# Revit family: 500_Slenderline_Sliding_Window_XOX_Standard
name_source: partatom
category: Windows
revit_build: Autodesk Revit 2014 (Build: 20130308_1515(x64)
units: mm (PartAtom-declared; Revit-internal decimal feet)

## types (56) — shared parameters
Centered In Wall = Yes
Custom Sash Width Middle = 500 mm  [stored 1.64042 ft]
Default Sill Height = 800 mm  [stored 2.62467 ft]
Description = Slenderline Sliding Window
Equal Sash Width = Yes
Frame Thickness = 54 mm
Heavy Duty Interlocker = No
Limit Sash Height Max = 1500 mm  [stored 4.92126 ft]
Limit Sash Height Min = 300 mm  [stored 0.984252 ft]
Limit Sash Width Max = 750 mm  [stored 2.46063 ft]
Limit Sash Width Min = 300 mm  [stored 0.984252 ft]
Limit Window Height Max = 1575 mm
Limit Window Height Min = 375 mm
Limit Window Width Max = 2270 mm  [stored 7.44751 ft]
Limit Window Width Min = 920 mm  [stored 3.01837 ft]
Manufacturer = Crealco
Model = 500
Sash Frame Seal = 1 mm  [stored 0.00328084 ft]
Sash Rail Fore Aft Spacing = 2 mm  [stored 0.00656168 ft]
Standard Interlocker = Yes
URL = www.crealco.co.za
Wall Closure = By host
zero-valued in all types: Custom Frame Offset From Exterior, Is Heavy Duty Mullion

## per-type parameters (varying)
| type | Area Middle Sash Glazing | Area Side Sash Glazing | Clearvue SHGC Value | Clearvue U Value | Custom Windload | Custom Window Height | Custom Window Width | Energy Advantage SHGC Value | Energy Advantage U Value | Height | Intruderprufe LowE SHGC Value | Intruderprufe LowE U Value | Intruderprufe SHGC Value | Intruderprufe U Value | Limit Sash Width Middle Max | Limit Sash Width Middle Min | Max Pane Area | Sash Height | Sash Width Middle | Sash Width Sides | Width | Windload Design |
| 500SW-0906XOX-1000Pa | 0.12 m² | 0.12 m² | 0.563 | 6.18 | 1000 mm  [stored 3.28084 ft] | 590 mm  [stored 1.9357 ft] | 890 mm  [stored 2.91995 ft] | 0.505 | 5.1 | 590 mm  [stored 1.9357 ft] | 0.427 | 4.69 | 0.534 | 6.05 | 300 mm  [stored 0.984252 ft] | 300 mm  [stored 0.984252 ft] | 0.12 m² | 515 mm | 300 mm  [stored 0.984252 ft] | 300 mm  [stored 0.984252 ft] | 920 mm  [stored 3.01837 ft] | 1000 mm  [stored 3.28084 ft] |
| 500SW-1206XOX-1000Pa | 0.16 m² | 0.16 m² | 0.578 | 6.19 | 1000 mm  [stored 3.28084 ft] | 590 mm  [stored 1.9357 ft] | 1190 mm  [stored 3.9042 ft] | 0.519 | 5 | 590 mm  [stored 1.9357 ft] | 0.439 | 4.7 | 0.549 | 6.06 | 570 mm  [stored 1.87008 ft] | 300 mm  [stored 0.984252 ft] | 0.16 m² | 515 mm | 390 mm | 390 mm | 1190 mm  [stored 3.9042 ft] | 1000 mm  [stored 3.28084 ft] |
| 500SW-1506XOX-1000Pa | 0.2 m² | 0.2 m² | 0.588 | 6.2 | 1000 mm  [stored 3.28084 ft] | 590 mm  [stored 1.9357 ft] | 1490 mm  [stored 4.88845 ft] | 0.527 | 4.93 | 590 mm  [stored 1.9357 ft] | 0.446 | 4.71 | 0.558 | 6.07 | 750 mm  [stored 2.46063 ft] | 300 mm  [stored 0.984252 ft] | 0.2 m² | 515 mm | 490 mm | 490 mm | 1490 mm  [stored 4.88845 ft] | 1000 mm  [stored 3.28084 ft] |
| 500SW-1806XOX-1000Pa | 0.25 m² | 0.25 m² | 0.594 | 6.2 | 1000 mm  [stored 3.28084 ft] | 590 mm  [stored 1.9357 ft] | 1790 mm  [stored 5.8727 ft] | 0.532 | 4.89 | 590 mm  [stored 1.9357 ft] | 0.451 | 4.71 | 0.564 | 6.07 | 750 mm  [stored 2.46063 ft] | 300 mm  [stored 0.984252 ft] | 0.25 m² | 515 mm | 590 mm  [stored 1.9357 ft] | 590 mm  [stored 1.9357 ft] | 1790 mm  [stored 5.8727 ft] | 1000 mm  [stored 3.28084 ft] |
| 500SW-2106XOX-1000Pa | 0.29 m² | 0.29 m² | 0.598 | 6.21 | 1000 mm  [stored 3.28084 ft] | 590 mm  [stored 1.9357 ft] | 2090 mm  [stored 6.85696 ft] | 0.536 | 4.86 | 590 mm  [stored 1.9357 ft] | 0.455 | 4.71 | 0.569 | 6.08 | 750 mm  [stored 2.46063 ft] | 570 mm  [stored 1.87008 ft] | 0.29 m² | 515 mm | 690 mm | 690 mm | 2090 mm  [stored 6.85696 ft] | 1000 mm  [stored 3.28084 ft] |
| 500SW-0909XOX-1000Pa | 0.2 m² | 0.2 m² | 0.631 | 6.09 | 1000 mm  [stored 3.28084 ft] | 890 mm  [stored 2.91995 ft] | 890 mm  [stored 2.91995 ft] | 0.566 | 4.88 | 890 mm  [stored 2.91995 ft] | 0.476 | 4.61 | 0.599 | 5.95 | 300 mm  [stored 0.984252 ft] | 300 mm  [stored 0.984252 ft] | 0.2 m² | 815 mm | 300 mm  [stored 0.984252 ft] | 300 mm  [stored 0.984252 ft] | 920 mm  [stored 3.01837 ft] | 1000 mm  [stored 3.28084 ft] |
| 500SW-1209XOX-1000Pa | 0.27 m² | 0.27 m² | 0.649 | 6.1 | 1000 mm  [stored 3.28084 ft] | 890 mm  [stored 2.91995 ft] | 1190 mm  [stored 3.9042 ft] | 0.581 | 4.75 | 890 mm  [stored 2.91995 ft] | 0.493 | 4.63 | 0.616 | 5.97 | 570 mm  [stored 1.87008 ft] | 300 mm  [stored 0.984252 ft] | 0.27 m² | 815 mm | 390 mm | 390 mm | 1190 mm  [stored 3.9042 ft] | 1000 mm  [stored 3.28084 ft] |
| 500SW-1509XOX-1000Pa | 0.34 m² | 0.34 m² | 0.659 | 6.1 | 1000 mm  [stored 3.28084 ft] | 890 mm  [stored 2.91995 ft] | 1490 mm  [stored 4.88845 ft] | 0.59 | 4.67 | 890 mm  [stored 2.91995 ft] | 0.501 | 4.63 | 0.626 | 5.97 | 750 mm  [stored 2.46063 ft] | 300 mm  [stored 0.984252 ft] | 0.34 m² | 815 mm | 490 mm | 490 mm | 1490 mm  [stored 4.88845 ft] | 1000 mm  [stored 3.28084 ft] |
| 500SW-1809XOX-1000Pa | 0.41 m² | 0.41 m² | 0.666 | 6.1 | 1000 mm  [stored 3.28084 ft] | 890 mm  [stored 2.91995 ft] | 1790 mm  [stored 5.8727 ft] | 0.596 | 4.62 | 890 mm  [stored 2.91995 ft] | 0.506 | 4.63 | 0.632 | 5.97 | 750 mm  [stored 2.46063 ft] | 300 mm  [stored 0.984252 ft] | 0.41 m² | 815 mm | 590 mm  [stored 1.9357 ft] | 590 mm  [stored 1.9357 ft] | 1790 mm  [stored 5.8727 ft] | 1000 mm  [stored 3.28084 ft] |
| 500SW-2109XOX-1000Pa | 0.49 m² | 0.49 m² | 0.671 | 6.1 | 1000 mm  [stored 3.28084 ft] | 890 mm  [stored 2.91995 ft] | 2090 mm  [stored 6.85696 ft] | 0.601 | 4.58 | 890 mm  [stored 2.91995 ft] | 0.51 | 4.63 | 0.637 | 5.97 | 750 mm  [stored 2.46063 ft] | 570 mm  [stored 1.87008 ft] | 0.49 m² | 815 mm | 690 mm | 690 mm | 2090 mm  [stored 6.85696 ft] | 1000 mm  [stored 3.28084 ft] |
| 500SW-0912XOX-1000Pa | 0.28 m² | 0.28 m² | 0.665 | 6.05 | 1000 mm  [stored 3.28084 ft] | 1190 mm  [stored 3.9042 ft] | 890 mm  [stored 2.91995 ft] | 0.596 | 4.77 | 1190 mm  [stored 3.9042 ft] | 0.505 | 4.59 | 0.631 | 5.92 | 300 mm  [stored 0.984252 ft] | 300 mm  [stored 0.984252 ft] | 0.28 m² | 1115 mm | 300 mm  [stored 0.984252 ft] | 300 mm  [stored 0.984252 ft] | 920 mm  [stored 3.01837 ft] | 1000 mm  [stored 3.28084 ft] |
| 500SW-1212XOX-1000Pa | 0.37 m² | 0.37 m² | 0.683 | 6.05 | 1000 mm  [stored 3.28084 ft] | 1190 mm  [stored 3.9042 ft] | 1190 mm  [stored 3.9042 ft] | 0.612 | 4.62 | 1190 mm  [stored 3.9042 ft] | 0.519 | 4.59 | 0.649 | 5.92 | 570 mm  [stored 1.87008 ft] | 300 mm  [stored 0.984252 ft] | 0.37 m² | 1115 mm | 390 mm | 390 mm | 1190 mm  [stored 3.9042 ft] | 1000 mm  [stored 3.28084 ft] |
| 500SW-1512XOX-1000Pa | 0.48 m² | 0.48 m² | 0.695 | 6.05 | 1000 mm  [stored 3.28084 ft] | 1190 mm  [stored 3.9042 ft] | 1490 mm  [stored 4.88845 ft] | 0.622 | 4.54 | 1190 mm  [stored 3.9042 ft] | 0.527 | 4.59 | 0.659 | 5.92 | 750 mm  [stored 2.46063 ft] | 300 mm  [stored 0.984252 ft] | 0.48 m² | 1115 mm | 490 mm | 490 mm | 1490 mm  [stored 4.88845 ft] | 1000 mm  [stored 3.28084 ft] |
| 500SW-1812XOX-1000Pa | 0.58 m² | 0.58 m² | 0.702 | 6.05 | 1000 mm  [stored 3.28084 ft] | 1190 mm  [stored 3.9042 ft] | 1790 mm  [stored 5.8727 ft] | 0.628 | 4.48 | 1190 mm  [stored 3.9042 ft] | 0.5333 | 4.59 | 0.666 | 5.92 | 750 mm  [stored 2.46063 ft] | 300 mm  [stored 0.984252 ft] | 0.58 m² | 1115 mm | 590 mm  [stored 1.9357 ft] | 590 mm  [stored 1.9357 ft] | 1790 mm  [stored 5.8727 ft] | 1000 mm  [stored 3.28084 ft] |
| 500SW-2112XOX-1000Pa | 0.69 m² | 0.69 m² | 0.707 | 6.05 | 1000 mm  [stored 3.28084 ft] | 1190 mm  [stored 3.9042 ft] | 2090 mm  [stored 6.85696 ft] | 0.633 | 4.44 | 1190 mm  [stored 3.9042 ft] | 0.537 | 4.59 | 0.671 | 5.92 | 750 mm  [stored 2.46063 ft] | 570 mm  [stored 1.87008 ft] | 0.69 m² | 1115 mm | 690 mm | 690 mm | 2090 mm  [stored 6.85696 ft] | 1000 mm  [stored 3.28084 ft] |
| 500SW-0915XOX-1000Pa | 0.36 m² | 0.36 m² | 0.685 | 6.02 | 1000 mm  [stored 3.28084 ft] | 1490 mm  [stored 4.88845 ft] | 890 mm  [stored 2.91995 ft] | 0.614 | 4.7 | 1490 mm  [stored 4.88845 ft] | 0.521 | 4.57 | 0.657 | 5.89 | 300 mm  [stored 0.984252 ft] | 300 mm  [stored 0.984252 ft] | 0.36 m² | 1415 mm  [stored 4.64239 ft] | 300 mm  [stored 0.984252 ft] | 300 mm  [stored 0.984252 ft] | 920 mm  [stored 3.01837 ft] | 1000 mm  [stored 3.28084 ft] |
| 500SW-1215XOX-1000Pa | 0.48 m² | 0.48 m² | 0.704 | 6.02 | 1000 mm  [stored 3.28084 ft] | 1490 mm  [stored 4.88845 ft] | 1190 mm  [stored 3.9042 ft] | 0.631 | 4.55 | 1490 mm  [stored 4.88845 ft] | 0.534 | 4.57 | 0.668 | 5.89 | 570 mm  [stored 1.87008 ft] | 300 mm  [stored 0.984252 ft] | 0.48 m² | 1415 mm  [stored 4.64239 ft] | 390 mm | 390 mm | 1190 mm  [stored 3.9042 ft] | 1000 mm  [stored 3.28084 ft] |
| 500SW-1515XOX-1000Pa | 0.61 m² | 0.61 m² | 0.716 | 6.02 | 1000 mm  [stored 3.28084 ft] | 1490 mm  [stored 4.88845 ft] | 1490 mm  [stored 4.88845 ft] | 0.64 | 4.46 | 1490 mm  [stored 4.88845 ft] | 0.543 | 4.57 | 0.679 | 5.89 | 750 mm  [stored 2.46063 ft] | 300 mm  [stored 0.984252 ft] | 0.61 m² | 1415 mm  [stored 4.64239 ft] | 490 mm | 490 mm | 1490 mm  [stored 4.88845 ft] | 1000 mm  [stored 3.28084 ft] |
| 500SW-1815XOX-1000Pa | 0.75 m² | 0.75 m² | 0.723 | 6.02 | 1000 mm  [stored 3.28084 ft] | 1490 mm  [stored 4.88845 ft] | 1790 mm  [stored 5.8727 ft] | 0.647 | 4.4 | 1490 mm  [stored 4.88845 ft] | 0.549 | 4.57 | 0.686 | 5.89 | 750 mm  [stored 2.46063 ft] | 300 mm  [stored 0.984252 ft] | 0.75 m² | 1415 mm  [stored 4.64239 ft] | 590 mm  [stored 1.9357 ft] | 590 mm  [stored 1.9357 ft] | 1790 mm  [stored 5.8727 ft] | 1000 mm  [stored 3.28084 ft] |
| 500SW-2115XOX-1000Pa | 0.88 m² | 0.88 m² | 0.729 | 6.02 | 1000 mm  [stored 3.28084 ft] | 1490 mm  [stored 4.88845 ft] | 2090 mm  [stored 6.85696 ft] | 0.652 | 4.35 | 1490 mm  [stored 4.88845 ft] | 0.533 | 4.57 | 0.691 | 5.89 | 750 mm  [stored 2.46063 ft] | 570 mm  [stored 1.87008 ft] | 0.88 m² | 1415 mm  [stored 4.64239 ft] | 690 mm | 690 mm | 2090 mm  [stored 6.85696 ft] | 1000 mm  [stored 3.28084 ft] |
| 500SW-0906XOX-1500Pa | 0.12 m² | 0.12 m² | 0.563 | 6.18 | 1500 mm  [stored 4.92126 ft] | 590 mm  [stored 1.9357 ft] | 890 mm  [stored 2.91995 ft] | 0.505 | 5.1 | 590 mm  [stored 1.9357 ft] | 0.427 | 4.69 | 0.534 | 6.05 | 300 mm  [stored 0.984252 ft] | 300 mm  [stored 0.984252 ft] | 0.12 m² | 515 mm | 300 mm  [stored 0.984252 ft] | 300 mm  [stored 0.984252 ft] | 920 mm  [stored 3.01837 ft] | 1500 mm  [stored 4.92126 ft] |
| 500SW-0906XOX-2000Pa | 0.12 m² | 0.12 m² | 0.563 | 6.18 | 2000 mm  [stored 6.56168 ft] | 590 mm  [stored 1.9357 ft] | 890 mm  [stored 2.91995 ft] | 0.505 | 5.1 | 590 mm  [stored 1.9357 ft] | 0.427 | 4.69 | 0.534 | 6.05 | 300 mm  [stored 0.984252 ft] | 300 mm  [stored 0.984252 ft] | 0.12 m² | 515 mm | 300 mm  [stored 0.984252 ft] | 300 mm  [stored 0.984252 ft] | 920 mm  [stored 3.01837 ft] | 2000 mm  [stored 6.56168 ft] |
| 500SW-0909XOX-1500Pa | 0.2 m² | 0.2 m² | 0.631 | 6.09 | 1500 mm  [stored 4.92126 ft] | 890 mm  [stored 2.91995 ft] | 890 mm  [stored 2.91995 ft] | 0.566 | 4.88 | 890 mm  [stored 2.91995 ft] | 0.476 | 4.61 | 0.599 | 5.95 | 300 mm  [stored 0.984252 ft] | 300 mm  [stored 0.984252 ft] | 0.2 m² | 815 mm | 300 mm  [stored 0.984252 ft] | 300 mm  [stored 0.984252 ft] | 920 mm  [stored 3.01837 ft] | 1500 mm  [stored 4.92126 ft] |
| 500SW-0909XOX-2000Pa | 0.2 m² | 0.2 m² | 0.631 | 6.09 | 2000 mm  [stored 6.56168 ft] | 890 mm  [stored 2.91995 ft] | 890 mm  [stored 2.91995 ft] | 0.566 | 4.88 | 890 mm  [stored 2.91995 ft] | 0.476 | 4.61 | 0.599 | 5.95 | 300 mm  [stored 0.984252 ft] | 300 mm  [stored 0.984252 ft] | 0.2 m² | 815 mm | 300 mm  [stored 0.984252 ft] | 300 mm  [stored 0.984252 ft] | 920 mm  [stored 3.01837 ft] | 2000 mm  [stored 6.56168 ft] |
| 500SW-0912XOX-1500Pa | 0.28 m² | 0.28 m² | 0.665 | 6.05 | 1500 mm  [stored 4.92126 ft] | 1190 mm  [stored 3.9042 ft] | 890 mm  [stored 2.91995 ft] | 0.596 | 4.77 | 1190 mm  [stored 3.9042 ft] | 0.505 | 4.59 | 0.631 | 5.92 | 300 mm  [stored 0.984252 ft] | 300 mm  [stored 0.984252 ft] | 0.28 m² | 1115 mm | 300 mm  [stored 0.984252 ft] | 300 mm  [stored 0.984252 ft] | 920 mm  [stored 3.01837 ft] | 1500 mm  [stored 4.92126 ft] |
| 500SW-0912XOX-2000Pa | 0.28 m² | 0.28 m² | 0.665 | 6.05 | 2000 mm  [stored 6.56168 ft] | 1190 mm  [stored 3.9042 ft] | 890 mm  [stored 2.91995 ft] | 0.596 | 4.77 | 1190 mm  [stored 3.9042 ft] | 0.505 | 4.59 | 0.631 | 5.92 | 300 mm  [stored 0.984252 ft] | 300 mm  [stored 0.984252 ft] | 0.28 m² | 1115 mm | 300 mm  [stored 0.984252 ft] | 300 mm  [stored 0.984252 ft] | 920 mm  [stored 3.01837 ft] | 2000 mm  [stored 6.56168 ft] |
| 500SW-0915XOX-1500Pa | 0.36 m² | 0.36 m² | 0.685 | 6.02 | 1500 mm  [stored 4.92126 ft] | 1490 mm  [stored 4.88845 ft] | 890 mm  [stored 2.91995 ft] | 0.614 | 4.7 | 1490 mm  [stored 4.88845 ft] | 0.521 | 4.57 | 0.657 | 5.89 | 300 mm  [stored 0.984252 ft] | 300 mm  [stored 0.984252 ft] | 0.36 m² | 1415 mm  [stored 4.64239 ft] | 300 mm  [stored 0.984252 ft] | 300 mm  [stored 0.984252 ft] | 920 mm  [stored 3.01837 ft] | 1500 mm  [stored 4.92126 ft] |
| 500SW-0915XOX-2000Pa | 0.36 m² | 0.36 m² | 0.685 | 6.02 | 2000 mm  [stored 6.56168 ft] | 1490 mm  [stored 4.88845 ft] | 890 mm  [stored 2.91995 ft] | 0.614 | 4.7 | 1490 mm  [stored 4.88845 ft] | 0.521 | 4.57 | 0.657 | 5.89 | 300 mm  [stored 0.984252 ft] | 300 mm  [stored 0.984252 ft] | 0.36 m² | 1415 mm  [stored 4.64239 ft] | 300 mm  [stored 0.984252 ft] | 300 mm  [stored 0.984252 ft] | 920 mm  [stored 3.01837 ft] | 2000 mm  [stored 6.56168 ft] |
| 500SW-1206XOX-1500Pa | 0.16 m² | 0.16 m² | 0.578 | 6.19 | 1500 mm  [stored 4.92126 ft] | 590 mm  [stored 1.9357 ft] | 1190 mm  [stored 3.9042 ft] | 0.519 | 5 | 590 mm  [stored 1.9357 ft] | 0.439 | 4.7 | 0.549 | 6.06 | 570 mm  [stored 1.87008 ft] | 300 mm  [stored 0.984252 ft] | 0.16 m² | 515 mm | 390 mm | 390 mm | 1190 mm  [stored 3.9042 ft] | 1500 mm  [stored 4.92126 ft] |
| 500SW-1206XOX-2000Pa | 0.16 m² | 0.16 m² | 0.578 | 6.19 | 2000 mm  [stored 6.56168 ft] | 590 mm  [stored 1.9357 ft] | 1190 mm  [stored 3.9042 ft] | 0.519 | 5 | 590 mm  [stored 1.9357 ft] | 0.439 | 4.7 | 0.549 | 6.06 | 570 mm  [stored 1.87008 ft] | 300 mm  [stored 0.984252 ft] | 0.16 m² | 515 mm | 390 mm | 390 mm | 1190 mm  [stored 3.9042 ft] | 2000 mm  [stored 6.56168 ft] |
| 500SW-1209XOX-1500Pa | 0.27 m² | 0.27 m² | 0.649 | 6.1 | 1500 mm  [stored 4.92126 ft] | 890 mm  [stored 2.91995 ft] | 1190 mm  [stored 3.9042 ft] | 0.581 | 4.75 | 890 mm  [stored 2.91995 ft] | 0.493 | 4.63 | 0.616 | 5.97 | 570 mm  [stored 1.87008 ft] | 300 mm  [stored 0.984252 ft] | 0.27 m² | 815 mm | 390 mm | 390 mm | 1190 mm  [stored 3.9042 ft] | 1500 mm  [stored 4.92126 ft] |
| 500SW-1209XOX-2000Pa | 0.27 m² | 0.27 m² | 0.649 | 6.1 | 2000 mm  [stored 6.56168 ft] | 890 mm  [stored 2.91995 ft] | 1190 mm  [stored 3.9042 ft] | 0.581 | 4.75 | 890 mm  [stored 2.91995 ft] | 0.493 | 4.63 | 0.616 | 5.97 | 570 mm  [stored 1.87008 ft] | 300 mm  [stored 0.984252 ft] | 0.27 m² | 815 mm | 390 mm | 390 mm | 1190 mm  [stored 3.9042 ft] | 2000 mm  [stored 6.56168 ft] |
| 500SW-1212XOX-1500Pa | 0.37 m² | 0.37 m² | 0.683 | 6.05 | 1500 mm  [stored 4.92126 ft] | 1190 mm  [stored 3.9042 ft] | 1190 mm  [stored 3.9042 ft] | 0.612 | 4.62 | 1190 mm  [stored 3.9042 ft] | 0.519 | 4.59 | 0.649 | 5.92 | 570 mm  [stored 1.87008 ft] | 300 mm  [stored 0.984252 ft] | 0.37 m² | 1115 mm | 390 mm | 390 mm | 1190 mm  [stored 3.9042 ft] | 1500 mm  [stored 4.92126 ft] |
| 500SW-1212XOX-2000Pa | 0.37 m² | 0.37 m² | 0.683 | 6.05 | 2000 mm  [stored 6.56168 ft] | 1190 mm  [stored 3.9042 ft] | 1190 mm  [stored 3.9042 ft] | 0.612 | 4.62 | 1190 mm  [stored 3.9042 ft] | 0.519 | 4.59 | 0.649 | 5.92 | 570 mm  [stored 1.87008 ft] | 300 mm  [stored 0.984252 ft] | 0.37 m² | 1115 mm | 390 mm | 390 mm | 1190 mm  [stored 3.9042 ft] | 2000 mm  [stored 6.56168 ft] |
| 500SW-1215XOX-1500Pa | 0.48 m² | 0.48 m² | 0.704 | 6.02 | 1500 mm  [stored 4.92126 ft] | 1490 mm  [stored 4.88845 ft] | 1190 mm  [stored 3.9042 ft] | 0.631 | 4.55 | 1490 mm  [stored 4.88845 ft] | 0.534 | 4.57 | 0.668 | 5.89 | 570 mm  [stored 1.87008 ft] | 300 mm  [stored 0.984252 ft] | 0.48 m² | 1415 mm  [stored 4.64239 ft] | 390 mm | 390 mm | 1190 mm  [stored 3.9042 ft] | 1500 mm  [stored 4.92126 ft] |
| 500SW-1215XOX-2000Pa | 0.48 m² | 0.48 m² | 0.704 | 6.02 | 2000 mm  [stored 6.56168 ft] | 1490 mm  [stored 4.88845 ft] | 1190 mm  [stored 3.9042 ft] | 0.631 | 4.55 | 1490 mm  [stored 4.88845 ft] | 0.534 | 4.57 | 0.668 | 5.89 | 570 mm  [stored 1.87008 ft] | 300 mm  [stored 0.984252 ft] | 0.48 m² | 1415 mm  [stored 4.64239 ft] | 390 mm | 390 mm | 1190 mm  [stored 3.9042 ft] | 2000 mm  [stored 6.56168 ft] |
| 500SW-1506XOX-1500Pa | 0.2 m² | 0.2 m² | 0.588 | 6.2 | 1500 mm  [stored 4.92126 ft] | 590 mm  [stored 1.9357 ft] | 1490 mm  [stored 4.88845 ft] | 0.527 | 4.93 | 590 mm  [stored 1.9357 ft] | 0.446 | 4.71 | 0.558 | 6.07 | 750 mm  [stored 2.46063 ft] | 300 mm  [stored 0.984252 ft] | 0.2 m² | 515 mm | 490 mm | 490 mm | 1490 mm  [stored 4.88845 ft] | 1500 mm  [stored 4.92126 ft] |
| 500SW-1506XOX-2000Pa | 0.2 m² | 0.2 m² | 0.588 | 6.2 | 2000 mm  [stored 6.56168 ft] | 590 mm  [stored 1.9357 ft] | 1490 mm  [stored 4.88845 ft] | 0.527 | 4.93 | 590 mm  [stored 1.9357 ft] | 0.446 | 4.71 | 0.558 | 6.07 | 750 mm  [stored 2.46063 ft] | 300 mm  [stored 0.984252 ft] | 0.2 m² | 515 mm | 490 mm | 490 mm | 1490 mm  [stored 4.88845 ft] | 2000 mm  [stored 6.56168 ft] |
| 500SW-1509XOX-1500Pa | 0.34 m² | 0.34 m² | 0.659 | 6.1 | 1500 mm  [stored 4.92126 ft] | 890 mm  [stored 2.91995 ft] | 1490 mm  [stored 4.88845 ft] | 0.59 | 4.67 | 890 mm  [stored 2.91995 ft] | 0.501 | 4.63 | 0.626 | 5.97 | 750 mm  [stored 2.46063 ft] | 300 mm  [stored 0.984252 ft] | 0.34 m² | 815 mm | 490 mm | 490 mm | 1490 mm  [stored 4.88845 ft] | 1500 mm  [stored 4.92126 ft] |
| 500SW-1509XOX-2000Pa | 0.34 m² | 0.34 m² | 0.659 | 6.1 | 2000 mm  [stored 6.56168 ft] | 890 mm  [stored 2.91995 ft] | 1490 mm  [stored 4.88845 ft] | 0.59 | 4.67 | 890 mm  [stored 2.91995 ft] | 0.501 | 4.63 | 0.626 | 5.97 | 750 mm  [stored 2.46063 ft] | 300 mm  [stored 0.984252 ft] | 0.34 m² | 815 mm | 490 mm | 490 mm | 1490 mm  [stored 4.88845 ft] | 2000 mm  [stored 6.56168 ft] |
| 500SW-1512XOX-1500Pa | 0.48 m² | 0.48 m² | 0.695 | 6.05 | 1500 mm  [stored 4.92126 ft] | 1190 mm  [stored 3.9042 ft] | 1490 mm  [stored 4.88845 ft] | 0.622 | 4.54 | 1190 mm  [stored 3.9042 ft] | 0.527 | 4.59 | 0.659 | 5.92 | 750 mm  [stored 2.46063 ft] | 300 mm  [stored 0.984252 ft] | 0.48 m² | 1115 mm | 490 mm | 490 mm | 1490 mm  [stored 4.88845 ft] | 1500 mm  [stored 4.92126 ft] |
| 500SW-1512XOX-2000Pa | 0.48 m² | 0.48 m² | 0.695 | 6.05 | 2000 mm  [stored 6.56168 ft] | 1190 mm  [stored 3.9042 ft] | 1490 mm  [stored 4.88845 ft] | 0.622 | 4.54 | 1190 mm  [stored 3.9042 ft] | 0.527 | 4.59 | 0.659 | 5.92 | 750 mm  [stored 2.46063 ft] | 300 mm  [stored 0.984252 ft] | 0.48 m² | 1115 mm | 490 mm | 490 mm | 1490 mm  [stored 4.88845 ft] | 2000 mm  [stored 6.56168 ft] |
| 500SW-1515XOX-1500Pa | 0.61 m² | 0.61 m² | 0.716 | 6.02 | 1500 mm  [stored 4.92126 ft] | 1490 mm  [stored 4.88845 ft] | 1490 mm  [stored 4.88845 ft] | 0.64 | 4.46 | 1490 mm  [stored 4.88845 ft] | 0.543 | 4.57 | 0.679 | 5.89 | 750 mm  [stored 2.46063 ft] | 300 mm  [stored 0.984252 ft] | 0.61 m² | 1415 mm  [stored 4.64239 ft] | 490 mm | 490 mm | 1490 mm  [stored 4.88845 ft] | 1500 mm  [stored 4.92126 ft] |
| 500SW-1806XOX-1500Pa | 0.25 m² | 0.25 m² | 0.594 | 6.2 | 1500 mm  [stored 4.92126 ft] | 590 mm  [stored 1.9357 ft] | 1790 mm  [stored 5.8727 ft] | 0.532 | 4.89 | 590 mm  [stored 1.9357 ft] | 0.451 | 4.71 | 0.564 | 6.07 | 750 mm  [stored 2.46063 ft] | 300 mm  [stored 0.984252 ft] | 0.25 m² | 515 mm | 590 mm  [stored 1.9357 ft] | 590 mm  [stored 1.9357 ft] | 1790 mm  [stored 5.8727 ft] | 1500 mm  [stored 4.92126 ft] |
| 500SW-1806XOX-2000Pa | 0.25 m² | 0.25 m² | 0.594 | 6.2 | 2000 mm  [stored 6.56168 ft] | 590 mm  [stored 1.9357 ft] | 1790 mm  [stored 5.8727 ft] | 0.532 | 4.89 | 590 mm  [stored 1.9357 ft] | 0.451 | 4.71 | 0.564 | 6.07 | 750 mm  [stored 2.46063 ft] | 300 mm  [stored 0.984252 ft] | 0.25 m² | 515 mm | 590 mm  [stored 1.9357 ft] | 590 mm  [stored 1.9357 ft] | 1790 mm  [stored 5.8727 ft] | 2000 mm  [stored 6.56168 ft] |
| 500SW-1809XOX-1500Pa | 0.41 m² | 0.41 m² | 0.666 | 6.1 | 1500 mm  [stored 4.92126 ft] | 890 mm  [stored 2.91995 ft] | 1790 mm  [stored 5.8727 ft] | 0.596 | 4.62 | 890 mm  [stored 2.91995 ft] | 0.506 | 4.63 | 0.632 | 5.97 | 750 mm  [stored 2.46063 ft] | 300 mm  [stored 0.984252 ft] | 0.41 m² | 815 mm | 590 mm  [stored 1.9357 ft] | 590 mm  [stored 1.9357 ft] | 1790 mm  [stored 5.8727 ft] | 1500 mm  [stored 4.92126 ft] |
| 500SW-1809XOX-2000Pa | 0.41 m² | 0.41 m² | 0.666 | 6.1 | 2000 mm  [stored 6.56168 ft] | 890 mm  [stored 2.91995 ft] | 1790 mm  [stored 5.8727 ft] | 0.596 | 4.62 | 890 mm  [stored 2.91995 ft] | 0.506 | 4.63 | 0.632 | 5.97 | 750 mm  [stored 2.46063 ft] | 300 mm  [stored 0.984252 ft] | 0.41 m² | 815 mm | 590 mm  [stored 1.9357 ft] | 590 mm  [stored 1.9357 ft] | 1790 mm  [stored 5.8727 ft] | 2000 mm  [stored 6.56168 ft] |
| 500SW-1812XOX-1500Pa | 0.58 m² | 0.58 m² | 0.702 | 6.05 | 1500 mm  [stored 4.92126 ft] | 1190 mm  [stored 3.9042 ft] | 1790 mm  [stored 5.8727 ft] | 0.628 | 4.48 | 1190 mm  [stored 3.9042 ft] | 0.5333 | 4.59 | 0.666 | 5.92 | 750 mm  [stored 2.46063 ft] | 300 mm  [stored 0.984252 ft] | 0.58 m² | 1115 mm | 590 mm  [stored 1.9357 ft] | 590 mm  [stored 1.9357 ft] | 1790 mm  [stored 5.8727 ft] | 1500 mm  [stored 4.92126 ft] |
| 500SW-1812XOX-2000Pa | 0.58 m² | 0.58 m² | 0.702 | 6.05 | 2000 mm  [stored 6.56168 ft] | 1190 mm  [stored 3.9042 ft] | 1790 mm  [stored 5.8727 ft] | 0.628 | 4.48 | 1190 mm  [stored 3.9042 ft] | 0.5333 | 4.59 | 0.666 | 5.92 | 750 mm  [stored 2.46063 ft] | 300 mm  [stored 0.984252 ft] | 0.58 m² | 1115 mm | 590 mm  [stored 1.9357 ft] | 590 mm  [stored 1.9357 ft] | 1790 mm  [stored 5.8727 ft] | 2000 mm  [stored 6.56168 ft] |
| 500SW-1815XOX-1500Pa | 0.75 m² | 0.75 m² | 0.723 | 6.02 | 1500 mm  [stored 4.92126 ft] | 1490 mm  [stored 4.88845 ft] | 1790 mm  [stored 5.8727 ft] | 0.647 | 4.4 | 1490 mm  [stored 4.88845 ft] | 0.549 | 4.57 | 0.686 | 5.89 | 750 mm  [stored 2.46063 ft] | 300 mm  [stored 0.984252 ft] | 0.75 m² | 1415 mm  [stored 4.64239 ft] | 590 mm  [stored 1.9357 ft] | 590 mm  [stored 1.9357 ft] | 1790 mm  [stored 5.8727 ft] | 1500 mm  [stored 4.92126 ft] |
| 500SW-2106XOX-1500Pa | 0.29 m² | 0.29 m² | 0.598 | 6.21 | 1500 mm  [stored 4.92126 ft] | 590 mm  [stored 1.9357 ft] | 2090 mm  [stored 6.85696 ft] | 0.536 | 4.86 | 590 mm  [stored 1.9357 ft] | 0.455 | 4.71 | 0.569 | 6.08 | 750 mm  [stored 2.46063 ft] | 570 mm  [stored 1.87008 ft] | 0.29 m² | 515 mm | 690 mm | 690 mm | 2090 mm  [stored 6.85696 ft] | 1500 mm  [stored 4.92126 ft] |
| 500SW-2106XOX-2000Pa | 0.29 m² | 0.29 m² | 0.598 | 6.21 | 2000 mm  [stored 6.56168 ft] | 590 mm  [stored 1.9357 ft] | 2090 mm  [stored 6.85696 ft] | 0.536 | 4.86 | 590 mm  [stored 1.9357 ft] | 0.455 | 4.71 | 0.569 | 6.08 | 750 mm  [stored 2.46063 ft] | 570 mm  [stored 1.87008 ft] | 0.29 m² | 515 mm | 690 mm | 690 mm | 2090 mm  [stored 6.85696 ft] | 2000 mm  [stored 6.56168 ft] |
| 500SW-2109XOX-1500Pa | 0.49 m² | 0.49 m² | 0.671 | 6.1 | 1500 mm  [stored 4.92126 ft] | 890 mm  [stored 2.91995 ft] | 2090 mm  [stored 6.85696 ft] | 0.601 | 4.58 | 890 mm  [stored 2.91995 ft] | 0.51 | 4.63 | 0.637 | 5.97 | 750 mm  [stored 2.46063 ft] | 570 mm  [stored 1.87008 ft] | 0.49 m² | 815 mm | 690 mm | 690 mm | 2090 mm  [stored 6.85696 ft] | 1500 mm  [stored 4.92126 ft] |
| 500SW-2109XOX-2000Pa | 0.49 m² | 0.49 m² | 0.671 | 6.1 | 2000 mm  [stored 6.56168 ft] | 890 mm  [stored 2.91995 ft] | 2090 mm  [stored 6.85696 ft] | 0.601 | 4.58 | 890 mm  [stored 2.91995 ft] | 0.51 | 4.63 | 0.637 | 5.97 | 750 mm  [stored 2.46063 ft] | 570 mm  [stored 1.87008 ft] | 0.49 m² | 815 mm | 690 mm | 690 mm | 2090 mm  [stored 6.85696 ft] | 2000 mm  [stored 6.56168 ft] |
| 500SW-2112XOX-1500Pa | 0.69 m² | 0.69 m² | 0.707 | 6.05 | 1500 mm  [stored 4.92126 ft] | 1190 mm  [stored 3.9042 ft] | 2090 mm  [stored 6.85696 ft] | 0.633 | 4.44 | 1190 mm  [stored 3.9042 ft] | 0.537 | 4.59 | 0.671 | 5.92 | 750 mm  [stored 2.46063 ft] | 570 mm  [stored 1.87008 ft] | 0.69 m² | 1115 mm | 690 mm | 690 mm | 2090 mm  [stored 6.85696 ft] | 1500 mm  [stored 4.92126 ft] |
| 500SW-2112XOX-2000Pa | 0.69 m² | 0.69 m² | 0.707 | 6.05 | 2000 mm  [stored 6.56168 ft] | 1190 mm  [stored 3.9042 ft] | 2090 mm  [stored 6.85696 ft] | 0.633 | 4.44 | 1190 mm  [stored 3.9042 ft] | 0.537 | 4.59 | 0.671 | 5.92 | 750 mm  [stored 2.46063 ft] | 570 mm  [stored 1.87008 ft] | 0.69 m² | 1115 mm | 690 mm | 690 mm | 2090 mm  [stored 6.85696 ft] | 2000 mm  [stored 6.56168 ft] |

note: [stored X ft] marks values corroborated as IEEE doubles in the binary element streams (Revit-internal decimal feet)

## geometry (parser evidence)
native form markers: Sweep x39
no freeform markers — native parametric forms only
